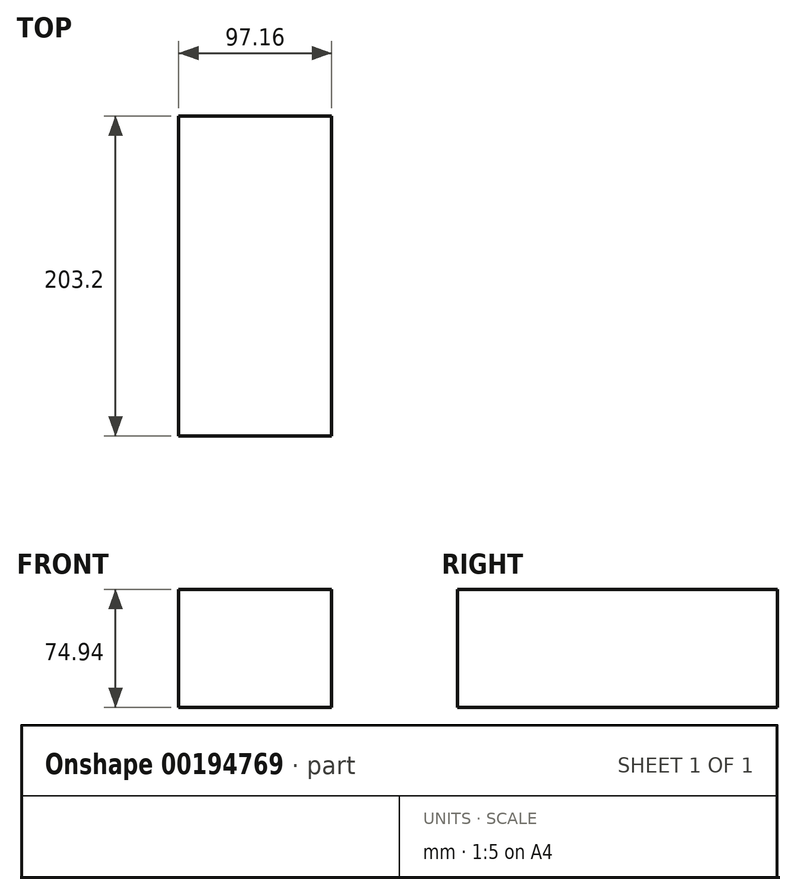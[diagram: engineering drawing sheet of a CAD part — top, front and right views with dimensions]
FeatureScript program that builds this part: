
annotation { "Feature Type Name" : "Feature", "Feature Type Description" : "" }
export const myFeature = defineFeature(function(context is Context, id is Id, definition is map)
    precondition{}
    {
        {
            var Q0;
            Q0=qCreatedBy(makeId("Front.planeOp"),FACE);
            var sketch = newSketch(context, id + "F0", { "sketchPlane" : qUnion([Q0])});
            skLineSegment(sketch, "E0.bottom", {"start": v(-48.58, 37.47) * mm, "end": v(48.58, 37.47) * mm});
            skLineSegment(sketch, "E0.top", {"start": v(-48.58, -37.47) * mm, "end": v(48.58, -37.47) * mm});
            skLineSegment(sketch, "E0.left", {"start": v(-48.58, 37.47) * mm, "end": v(-48.58, -37.47) * mm});
            skLineSegment(sketch, "E0.right", {"start": v(48.58, 37.47) * mm, "end": v(48.58, -37.47) * mm});
            skPoint(sketch, "E0.middle", {"position": v(0, 0) * mm});
            skSolve(sketch);
        }
        {
            var Q0;
            Q0 = qSketchRegion(id + "F0", true);
            extrude(context, id + "F1", {"entities" : qUnion([Q0]), "depth" : 101.6 * mm, "hasSecondDirection" : true, "secondDirectionOppositeDirection" : true, "secondDirectionDepth" : 101.6 * mm});
        }
    });
